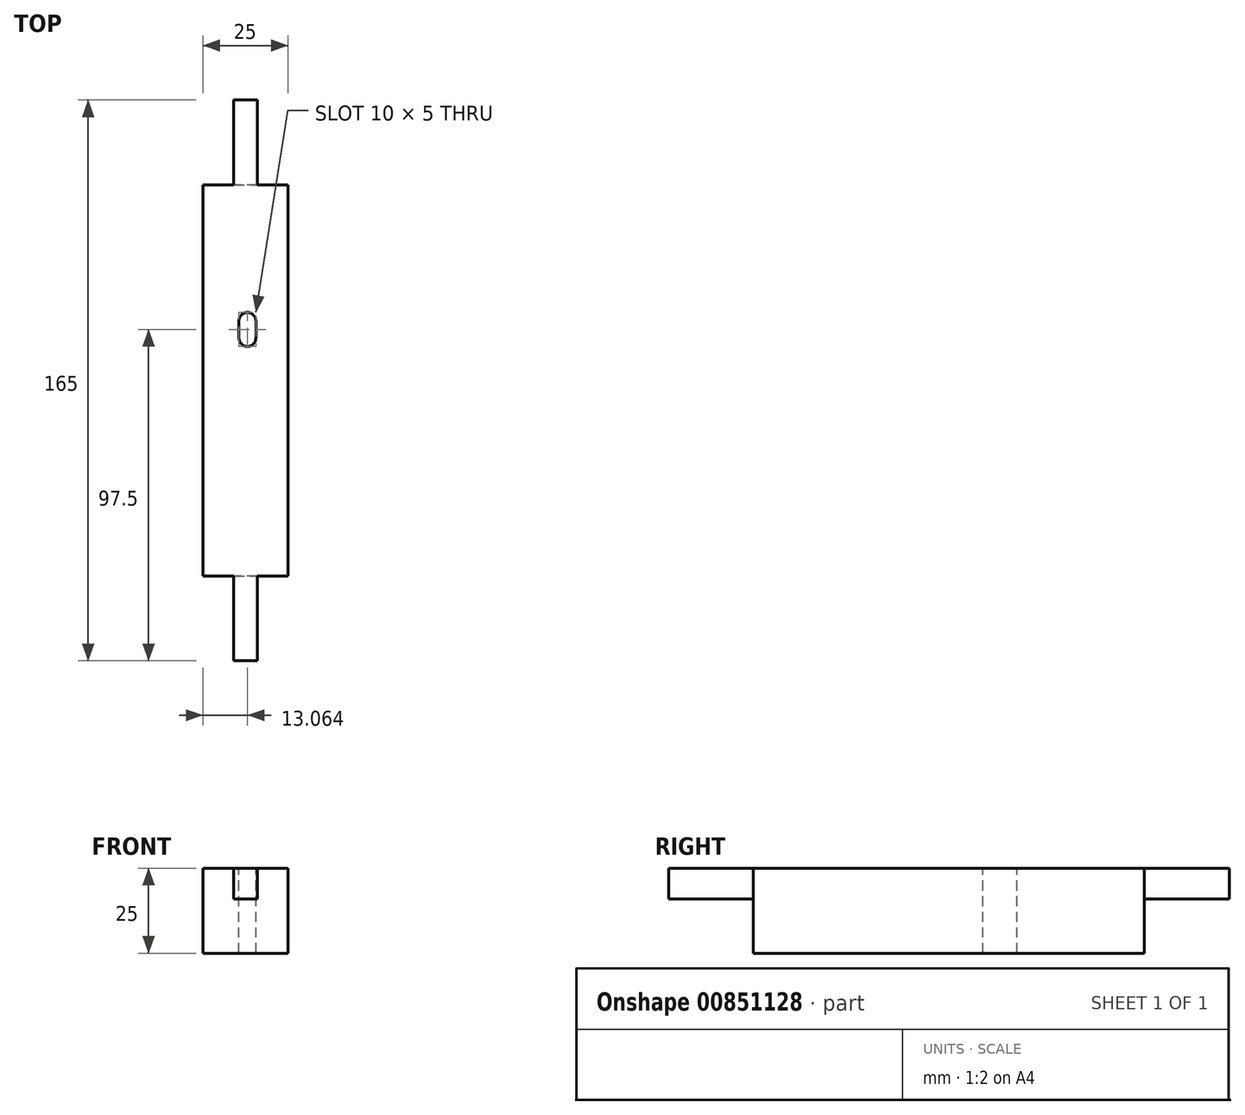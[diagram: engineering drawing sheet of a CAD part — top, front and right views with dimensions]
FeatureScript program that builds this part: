
annotation { "Feature Type Name" : "Feature", "Feature Type Description" : "" }
export const myFeature = defineFeature(function(context is Context, id is Id, definition is map)
    precondition{}
    {
        {
            var Q0;
            Q0=qCreatedBy(makeId("Front.planeOp"),FACE);
            var sketch = newSketch(context, id + "F0", { "sketchPlane" : qUnion([Q0])});
            skLineSegment(sketch, "E0.bottom", {"start": v(-7.82, 14.87) * mm, "end": v(17.18, 14.87) * mm});
            skLineSegment(sketch, "E0.top", {"start": v(-7.82, -10.13) * mm, "end": v(17.18, -10.13) * mm});
            skLineSegment(sketch, "E0.left", {"start": v(-7.82, 14.87) * mm, "end": v(-7.82, -10.13) * mm});
            skLineSegment(sketch, "E0.right", {"start": v(17.18, 14.87) * mm, "end": v(17.18, -10.13) * mm});
            skSolve(sketch);
        }
        {
            var Q0;
            Q0 = qSketchRegion(id + "F0", true);
            extrude(context, id + "F1", {"entities" : qUnion([Q0]), "depth" : 115 * mm, "offsetDistance" : 25 * mm});
        }
        {
            var Q0;
            Q0=makeQuery(id+"F1.opExtrude","CAP_FACE",FACE,{"disambiguationData":[OSD([sQuery(id+"F0.wireOp",EDGE,"E0.bottom"),sQuery(id+"F0.wireOp",EDGE,"E0.top"),sQuery(id+"F0.wireOp",EDGE,"E0.left"),sQuery(id+"F0.wireOp",EDGE,"E0.right")])],"isStart":false});
            var sketch = newSketch(context, id + "F2", { "sketchPlane" : qUnion([Q0])});
            skLineSegment(sketch, "E1.bottom", {"start": v(1.23, 14.87) * mm, "end": v(8.13, 14.87) * mm});
            skLineSegment(sketch, "E1.top", {"start": v(1.23, 5.87) * mm, "end": v(8.13, 5.87) * mm});
            skLineSegment(sketch, "E1.left", {"start": v(1.23, 14.87) * mm, "end": v(1.23, 5.87) * mm});
            skLineSegment(sketch, "E1.right", {"start": v(8.13, 14.87) * mm, "end": v(8.13, 5.87) * mm});
            skSolve(sketch);
        }
        {
            var Q0;
            Q0 = qSketchRegion(id + "F2", true);
            extrude(context, id + "F3", {"entities" : qUnion([Q0]), "operationType" : NewBodyOperationType.ADD, "depth" : 25 * mm, "offsetDistance" : 25 * mm, "hasSecondDirection" : true, "secondDirectionOppositeDirection" : true, "secondDirectionDepth" : 140 * mm});
        }
        {
            var Q0;
            Q0=makeQuery(id+"F3.boolean.opBoolean","MERGE",FACE,{"derivedFrom":[makeQuery(id+"F1.opExtrude","SWEPT_FACE",FACE,{"disambiguationData":[OSD([sQuery(id+"F0.wireOp",EDGE,"E0.bottom")])]}),makeQuery(id+"F3.opExtrude","SWEPT_FACE",FACE,{"disambiguationData":[OSD([sQuery(id+"F2.wireOp",EDGE,"E1.bottom")])]})]});
            var sketch = newSketch(context, id + "F4", { "sketchPlane" : qUnion([Q0])});
            skLineSegment(sketch, "E2.left", {"start": v(2.74, -40) * mm, "end": v(2.74, -45) * mm});
            skLineSegment(sketch, "E2.right", {"start": v(7.74, -40) * mm, "end": v(7.74, -45) * mm});
            skArc(sketch, "E3", {"start": v(7.74, -40) * mm, "mid": v(5.24, -37.5) * mm, "end": v(2.74, -40) * mm});
            skArc(sketch, "E4", {"start": v(2.74, -45) * mm, "mid": v(5.24, -47.5) * mm, "end": v(7.74, -45) * mm});
            skSolve(sketch);
        }
        {
            var Q0;
            Q0 = qSketchRegion(id + "F4", true);
            extrude(context, id + "F5", {"entities" : qUnion([Q0]), "operationType" : NewBodyOperationType.REMOVE, "oppositeDirection" : true, "depth" : 26 * mm, "offsetDistance" : 25 * mm});
        }
    });
